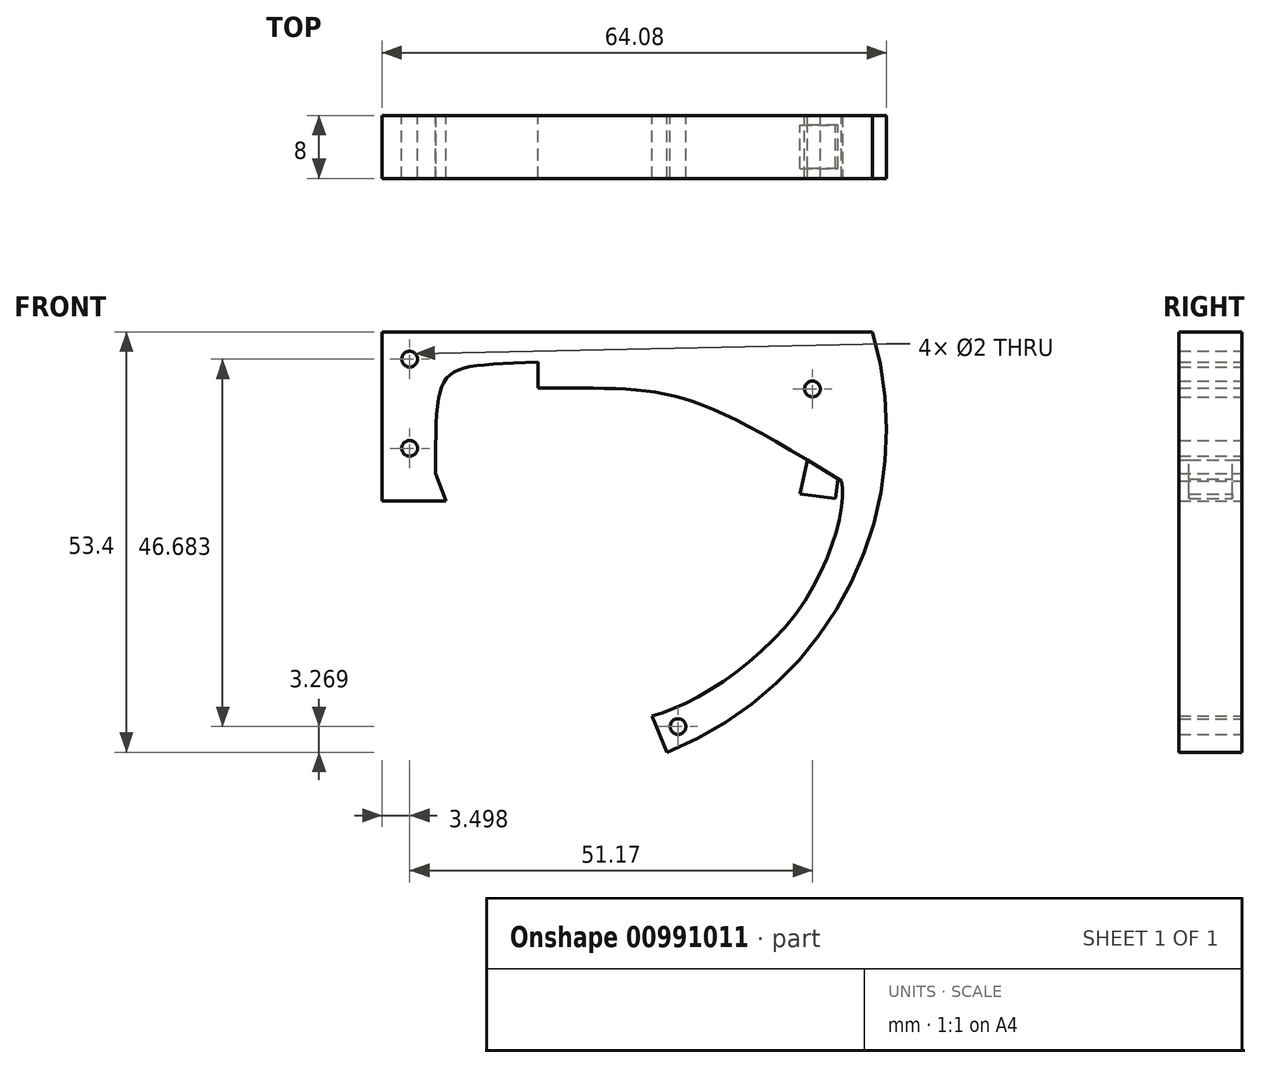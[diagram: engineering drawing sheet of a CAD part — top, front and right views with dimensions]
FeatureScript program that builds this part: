
annotation { "Feature Type Name" : "Feature", "Feature Type Description" : "" }
export const myFeature = defineFeature(function(context is Context, id is Id, definition is map)
    precondition{}
    {
        {
            var Q0;
            Q0=qCreatedBy(makeId("Front.planeOp"),FACE);
            var sketch = newSketch(context, id + "F0", { "sketchPlane" : qUnion([Q0])});
            skLineSegment(sketch, "E0", {"start": v(0, 21.44) * mm, "end": v(62.3, 21.44) * mm});
            skLineSegment(sketch, "E1", {"start": v(34.3, -27.32) * mm, "end": v(36.18, -31.96) * mm});
            skArc(sketch, "E2", {"start": v(36.18, -31.96) * mm, "mid": v(59.6, -10.33) * mm, "end": v(62.3, 21.44) * mm});
            skCircle(sketch, "E3", {"center": v(3.5, 18) * mm, "radius": 1 * mm});
            skCircle(sketch, "E4", {"center": v(3.5, 6.66) * mm, "radius": 1 * mm});
            skCircle(sketch, "E5", {"center": v(54.67, 14.2) * mm, "radius": 1 * mm});
            skCircle(sketch, "E6", {"center": v(37.59, -28.7) * mm, "radius": 1 * mm});
            skLineSegment(sketch, "E7", {"start": v(0, 21.44) * mm, "end": v(0, 3.73) * mm});
            skFitSpline(sketch, "E8", {"points": [v(34.3, -27.32) * mm, v(52.88, -13.89) * mm, v(58.33, 2.5) * mm], "startDerivative": vector(28.58, 7.3) * mm, "endDerivative": vector(-4.8, 17.89) * mm});
            skLineSegment(sketch, "E9", {"start": v(58.33, 2.5) * mm, "end": v(54.05, 5.15) * mm});
            skLineSegment(sketch, "E10", {"start": v(53.1, 0.89) * mm, "end": v(57.56, 0.3) * mm});
            skLineSegment(sketch, "E11", {"start": v(53.1, 0.89) * mm, "end": v(54.05, 5.15) * mm});
            skLineSegment(sketch, "E12", {"start": v(0, 0) * mm, "end": v(0, 3.73) * mm});
            skLineSegment(sketch, "E13", {"start": v(54.05, 5.15) * mm, "end": v(54.05, 5.15) * mm});
            skLineSegment(sketch, "E14", {"start": v(6.8, 3.48) * mm, "end": v(8.15, 0) * mm});
            skLineSegment(sketch, "E15", {"start": v(0, 0) * mm, "end": v(8.15, 0) * mm});
            skFitSpline(sketch, "E16", {"points": [v(19.84, 17.65) * mm, v(6.8, 3.48) * mm], "startDerivative": vector(-39.16, -2.2) * mm, "endDerivative": vector(0.06, -44.05) * mm});
            skFitSpline(sketch, "E17", {"points": [v(54.05, 5.15) * mm, v(19.83, 14.33) * mm], "startDerivative": vector(-49.64, 30.04) * mm, "endDerivative": vector(-45.98, 0.45) * mm});
            skLineSegment(sketch, "E18", {"start": v(57.56, 0.3) * mm, "end": v(57.89, 2.77) * mm});
            skLineSegment(sketch, "E19", {"start": v(19.83, 14.33) * mm, "end": v(19.84, 17.65) * mm});
            skLineSegment(sketch, "E20", {"start": v(8.15, 0) * mm, "end": v(9.15, 0) * mm, "construction": true});
            skSolve(sketch);
        }
        {
            var Q0;
            Q0=makeQuery(id+"F0.imprint","IMPRINT",FACE,{"disambiguationData":[TD([[makeQuery(id+"F0.imprint","IMPRINT",EDGE,{"derivedFrom":sQuery(id+"F0.wireOp",EDGE,"E0")}),-1.0]])]});
            extrude(context, id + "F1", {"entities" : qUnion([Q0]), "endBound" : BoundingType.SYMMETRIC, "depth" : 8 * mm, "offsetDistance" : 25 * mm});
        }
        {
            var Q0;
            Q0=makeQuery(id+"F0.imprint","IMPRINT",FACE,{"disambiguationData":[TD([[makeQuery(id+"F0.imprint","IMPRINT",EDGE,{"derivedFrom":sQuery(id+"F0.wireOp",EDGE,"E10")}),1.0]])]});
            extrude(context, id + "F2", {"entities" : qUnion([Q0]), "operationType" : NewBodyOperationType.ADD, "endBound" : BoundingType.SYMMETRIC, "depth" : 5.5 * mm, "offsetDistance" : 25 * mm});
        }
    });
